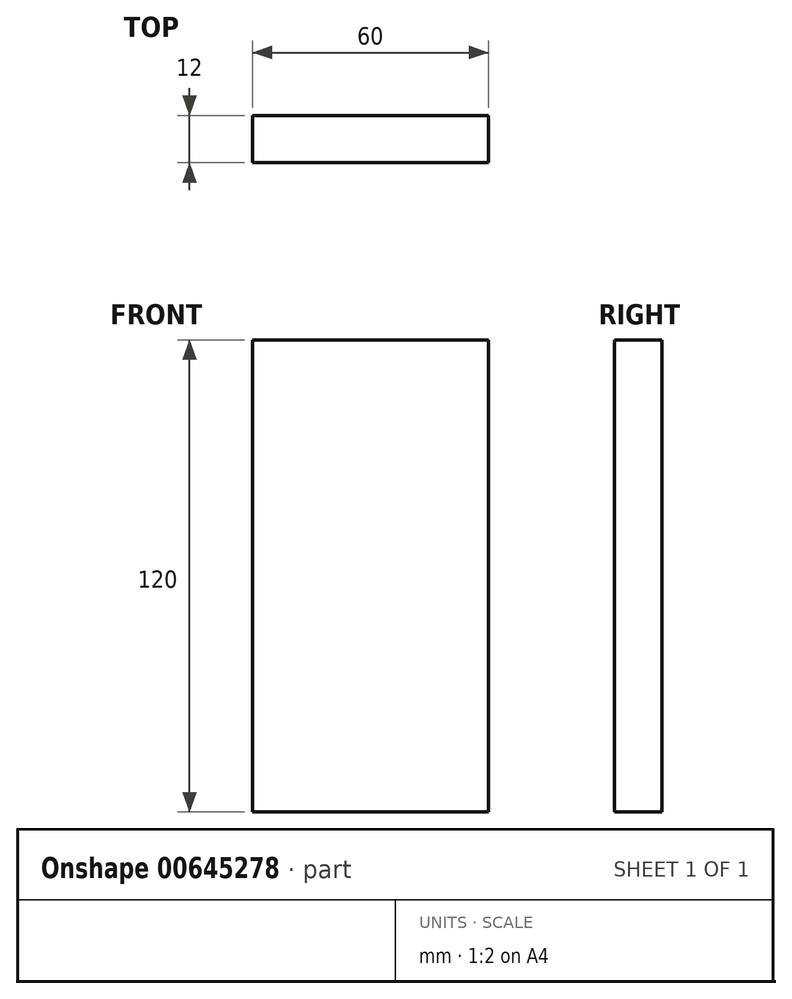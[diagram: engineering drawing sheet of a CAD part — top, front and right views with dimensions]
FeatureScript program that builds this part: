
annotation { "Feature Type Name" : "Feature", "Feature Type Description" : "" }
export const myFeature = defineFeature(function(context is Context, id is Id, definition is map)
    precondition{}
    {
        {
            var Q0;
            Q0=qCreatedBy(makeId("Front.planeOp"),FACE);
            var sketch = newSketch(context, id + "F0", { "sketchPlane" : qUnion([Q0])});
            skLineSegment(sketch, "E0.bottom", {"start": v(30, -60) * mm, "end": v(-30, -60) * mm});
            skLineSegment(sketch, "E0.top", {"start": v(30, 60) * mm, "end": v(-30, 60) * mm});
            skLineSegment(sketch, "E0.left", {"start": v(30, -60) * mm, "end": v(30, 60) * mm});
            skLineSegment(sketch, "E0.right", {"start": v(-30, -60) * mm, "end": v(-30, 60) * mm});
            skPoint(sketch, "E0.middle", {"position": v(0, 0) * mm});
            skSolve(sketch);
        }
        {
            var Q0;
            Q0 = qSketchRegion(id + "F0", true);
            extrude(context, id + "F1", {"entities" : qUnion([Q0]), "depth" : 12 * mm, "offsetDistance" : 25 * mm});
        }
    });
